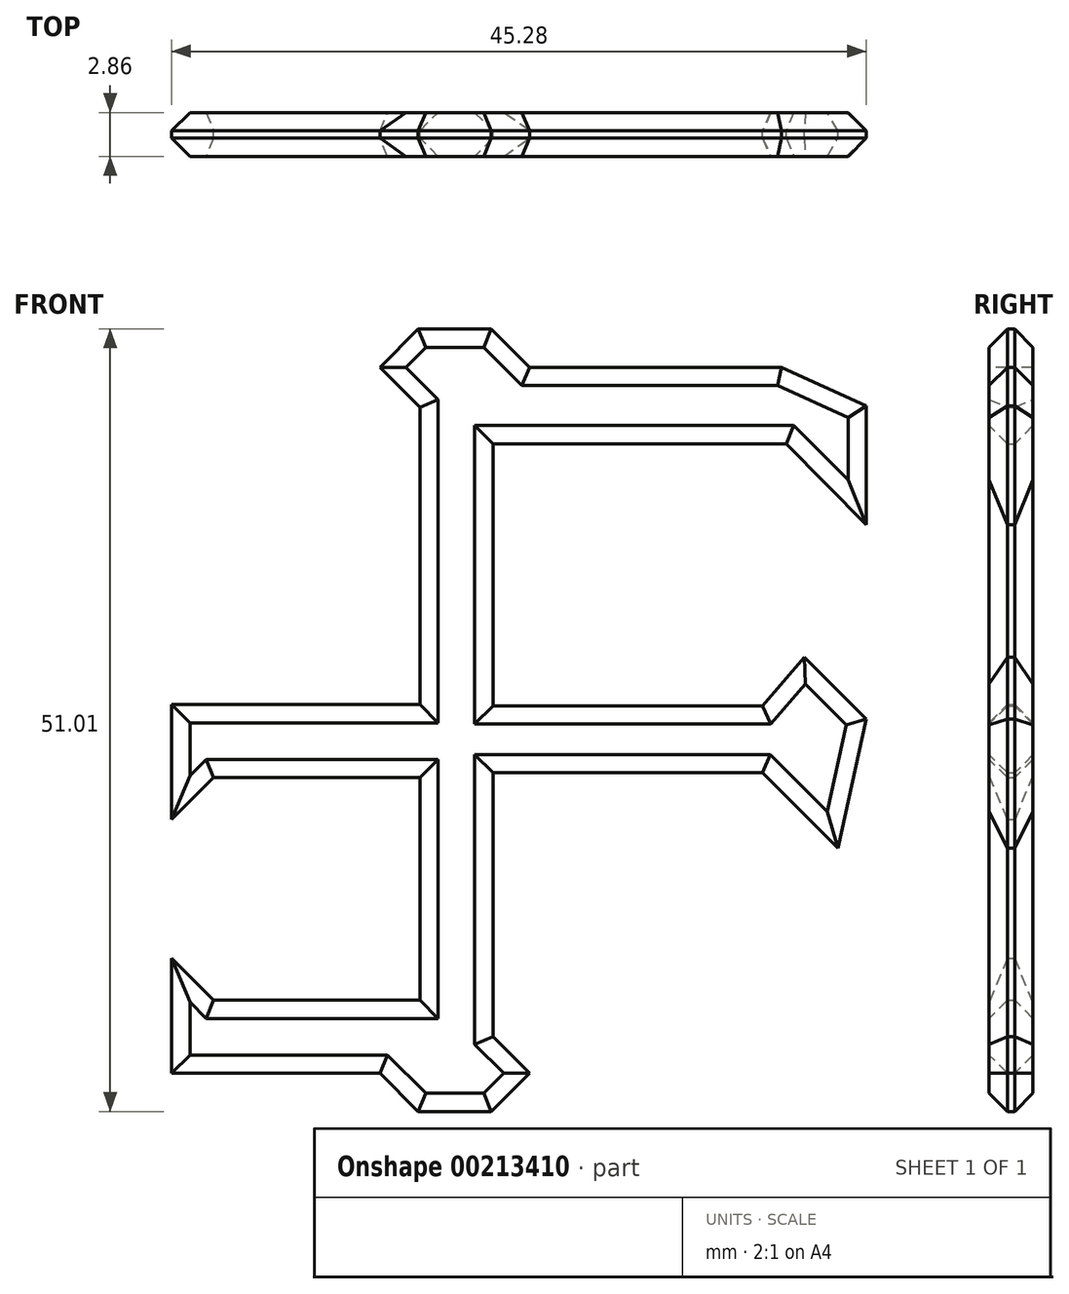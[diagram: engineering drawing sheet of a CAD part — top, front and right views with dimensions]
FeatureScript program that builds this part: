
annotation { "Feature Type Name" : "Feature", "Feature Type Description" : "" }
export const myFeature = defineFeature(function(context is Context, id is Id, definition is map)
    precondition{}
    {
        {
            var Q0;
            Q0=qCreatedBy(makeId("Front.planeOp"),FACE);
            var sketch = newSketch(context, id + "F0", { "sketchPlane" : qUnion([Q0])});
            skLineSegment(sketch, "E0", {"start": v(-3.18, 25.96) * mm, "end": v(-6.65, 29.43) * mm});
            skLineSegment(sketch, "E1", {"start": v(6.35, 29.43) * mm, "end": v(28.26, 29.43) * mm});
            skLineSegment(sketch, "E2", {"start": v(28.26, 29.43) * mm, "end": v(35.62, 26.07) * mm});
            skLineSegment(sketch, "E3", {"start": v(35.62, 15.75) * mm, "end": v(28.66, 22.79) * mm});
            skLineSegment(sketch, "E4", {"start": v(28.66, 22.79) * mm, "end": v(3.17, 22.79) * mm});
            skLineSegment(sketch, "E5", {"start": v(3.17, 22.79) * mm, "end": v(3.18, 0) * mm});
            skLineSegment(sketch, "E6", {"start": v(3.18, 0) * mm, "end": v(26.6, 0) * mm});
            skLineSegment(sketch, "E7", {"start": v(26.6, 0) * mm, "end": v(30.23, 4.24) * mm});
            skLineSegment(sketch, "E8", {"start": v(30.23, 4.24) * mm, "end": v(35.62, -1.15) * mm});
            skLineSegment(sketch, "E9", {"start": v(35.62, -1.15) * mm, "end": v(33.14, -12.36) * mm});
            skLineSegment(sketch, "E10", {"start": v(33.14, -12.36) * mm, "end": v(26.6, -5.82) * mm});
            skLineSegment(sketch, "E11", {"start": v(26.6, -5.82) * mm, "end": v(3.18, -5.82) * mm});
            skLineSegment(sketch, "E12", {"start": v(3.18, -5.82) * mm, "end": v(3.18, -28.75) * mm});
            skLineSegment(sketch, "E13", {"start": v(3.18, -28.75) * mm, "end": v(6.35, -31.93) * mm});
            skLineSegment(sketch, "E14", {"start": v(-6.65, 29.43) * mm, "end": v(-3.32, 32.76) * mm});
            skPoint(sketch, "E14.endSnap0", {"position": v(-3.32, 26.11) * mm});
            skLineSegment(sketch, "E15", {"start": v(-3.32, 32.76) * mm, "end": v(3.03, 32.76) * mm});
            skLineSegment(sketch, "E16", {"start": v(3.03, 32.76) * mm, "end": v(6.35, 29.43) * mm});
            skPoint(sketch, "E17.startSnap0", {"position": v(2.15, -36.37) * mm});
            skLineSegment(sketch, "E18", {"start": v(-6.65, -31.93) * mm, "end": v(-22.13, -31.93) * mm});
            skLineSegment(sketch, "E19", {"start": v(-22.13, -31.93) * mm, "end": v(-24.74, -31.93) * mm});
            skLineSegment(sketch, "E20", {"start": v(-24.74, -31.93) * mm, "end": v(-24.74, -21.93) * mm});
            skLineSegment(sketch, "E21", {"start": v(-24.74, -21.93) * mm, "end": v(-21.1, -25.58) * mm});
            skLineSegment(sketch, "E22", {"start": v(-21.1, -25.58) * mm, "end": v(-3.17, -25.58) * mm});
            skLineSegment(sketch, "E23", {"start": v(-3.17, -25.58) * mm, "end": v(-3.18, -6.24) * mm});
            skLineSegment(sketch, "E24", {"start": v(-3.18, -6.24) * mm, "end": v(-21.1, -6.24) * mm});
            skLineSegment(sketch, "E25", {"start": v(-21.1, -6.24) * mm, "end": v(-24.74, -9.88) * mm});
            skLineSegment(sketch, "E26", {"start": v(-24.74, -9.88) * mm, "end": v(-24.74, 0.11) * mm});
            skLineSegment(sketch, "E27", {"start": v(-24.74, 0.11) * mm, "end": v(-3.17, 0.11) * mm});
            skLineSegment(sketch, "E28", {"start": v(0, 22.79) * mm, "end": v(0, 0.11) * mm});
            skLineSegment(sketch, "E29", {"start": v(-3.18, 25.96) * mm, "end": v(-3.17, 0.11) * mm});
            skLineSegment(sketch, "E30", {"start": v(-6.65, -31.93) * mm, "end": v(-3.32, -35.25) * mm});
            skLineSegment(sketch, "E31", {"start": v(-3.32, -35.25) * mm, "end": v(3.03, -35.25) * mm});
            skLineSegment(sketch, "E32", {"start": v(3.03, -35.25) * mm, "end": v(6.35, -31.93) * mm});
            skPoint(sketch, "E33.orphan", {"position": v(-3.17, -31.93) * mm});
            skLineSegment(sketch, "E34", {"start": v(35.62, 26.07) * mm, "end": v(35.62, 15.75) * mm});
            skSolve(sketch);
        }
        {
            var Q0;
            Q0=makeQuery(id+"F0.imprint","IMPRINT",FACE,{"disambiguationData":[TD([[makeQuery(id+"F0.imprint","IMPRINT",EDGE,{"derivedFrom":sQuery(id+"F0.wireOp",EDGE,"E0")}),-1.0]])]});
            extrude(context, id + "F1", {"entities" : qUnion([Q0]), "depth" : 3.8 * mm});
        }
        {
            var Q0;
            Q0=makeQuery(id+"F1.opExtrude","CAP_FACE",FACE,{"disambiguationData":[OSD([sQuery(id+"F0.wireOp",EDGE,"E0"),sQuery(id+"F0.wireOp",EDGE,"E1"),sQuery(id+"F0.wireOp",EDGE,"E2"),sQuery(id+"F0.wireOp",EDGE,"E3"),sQuery(id+"F0.wireOp",EDGE,"E4"),sQuery(id+"F0.wireOp",EDGE,"E5"),sQuery(id+"F0.wireOp",EDGE,"E6"),sQuery(id+"F0.wireOp",EDGE,"E7"),sQuery(id+"F0.wireOp",EDGE,"E8"),sQuery(id+"F0.wireOp",EDGE,"E9"),sQuery(id+"F0.wireOp",EDGE,"E10"),sQuery(id+"F0.wireOp",EDGE,"E11"),sQuery(id+"F0.wireOp",EDGE,"E12"),sQuery(id+"F0.wireOp",EDGE,"E13"),sQuery(id+"F0.wireOp",EDGE,"E14"),sQuery(id+"F0.wireOp",EDGE,"E15"),sQuery(id+"F0.wireOp",EDGE,"E16"),sQuery(id+"F0.wireOp",EDGE,"E18"),sQuery(id+"F0.wireOp",EDGE,"E19"),sQuery(id+"F0.wireOp",EDGE,"E20"),sQuery(id+"F0.wireOp",EDGE,"E21"),sQuery(id+"F0.wireOp",EDGE,"E22"),sQuery(id+"F0.wireOp",EDGE,"E23"),sQuery(id+"F0.wireOp",EDGE,"E24"),sQuery(id+"F0.wireOp",EDGE,"E25"),sQuery(id+"F0.wireOp",EDGE,"E26"),sQuery(id+"F0.wireOp",EDGE,"E27"),sQuery(id+"F0.wireOp",EDGE,"E29"),sQuery(id+"F0.wireOp",EDGE,"E30"),sQuery(id+"F0.wireOp",EDGE,"E31"),sQuery(id+"F0.wireOp",EDGE,"E32"),sQuery(id+"F0.wireOp",EDGE,"E34")])],"isStart":false});
            var Q1;
            Q1=makeQuery(id+"F1.opExtrude","CAP_FACE",FACE,{"disambiguationData":[OSD([sQuery(id+"F0.wireOp",EDGE,"E0"),sQuery(id+"F0.wireOp",EDGE,"E1"),sQuery(id+"F0.wireOp",EDGE,"E2"),sQuery(id+"F0.wireOp",EDGE,"E3"),sQuery(id+"F0.wireOp",EDGE,"E4"),sQuery(id+"F0.wireOp",EDGE,"E5"),sQuery(id+"F0.wireOp",EDGE,"E6"),sQuery(id+"F0.wireOp",EDGE,"E7"),sQuery(id+"F0.wireOp",EDGE,"E8"),sQuery(id+"F0.wireOp",EDGE,"E9"),sQuery(id+"F0.wireOp",EDGE,"E10"),sQuery(id+"F0.wireOp",EDGE,"E11"),sQuery(id+"F0.wireOp",EDGE,"E12"),sQuery(id+"F0.wireOp",EDGE,"E13"),sQuery(id+"F0.wireOp",EDGE,"E14"),sQuery(id+"F0.wireOp",EDGE,"E15"),sQuery(id+"F0.wireOp",EDGE,"E16"),sQuery(id+"F0.wireOp",EDGE,"E18"),sQuery(id+"F0.wireOp",EDGE,"E19"),sQuery(id+"F0.wireOp",EDGE,"E20"),sQuery(id+"F0.wireOp",EDGE,"E21"),sQuery(id+"F0.wireOp",EDGE,"E22"),sQuery(id+"F0.wireOp",EDGE,"E23"),sQuery(id+"F0.wireOp",EDGE,"E24"),sQuery(id+"F0.wireOp",EDGE,"E25"),sQuery(id+"F0.wireOp",EDGE,"E26"),sQuery(id+"F0.wireOp",EDGE,"E27"),sQuery(id+"F0.wireOp",EDGE,"E29"),sQuery(id+"F0.wireOp",EDGE,"E30"),sQuery(id+"F0.wireOp",EDGE,"E31"),sQuery(id+"F0.wireOp",EDGE,"E32"),sQuery(id+"F0.wireOp",EDGE,"E34")])],"isStart":true});
            chamfer(context, id + "F2", {"entities" : qUnion([Q0, Q1]), "width" : 1.59 * mm, "tangentPropagation" : true});
        }
        {
            var Q0;
            Q0=makeQuery(id+"F1.opExtrude","SWEPT_BODY",BODY,{"disambiguationData":[OSD([sQuery(id+"F0.wireOp",EDGE,"E0"),sQuery(id+"F0.wireOp",EDGE,"E1"),sQuery(id+"F0.wireOp",EDGE,"E2"),sQuery(id+"F0.wireOp",EDGE,"E3"),sQuery(id+"F0.wireOp",EDGE,"E4"),sQuery(id+"F0.wireOp",EDGE,"E5"),sQuery(id+"F0.wireOp",EDGE,"E6"),sQuery(id+"F0.wireOp",EDGE,"E7"),sQuery(id+"F0.wireOp",EDGE,"E8"),sQuery(id+"F0.wireOp",EDGE,"E9"),sQuery(id+"F0.wireOp",EDGE,"E10"),sQuery(id+"F0.wireOp",EDGE,"E11"),sQuery(id+"F0.wireOp",EDGE,"E12"),sQuery(id+"F0.wireOp",EDGE,"E13"),sQuery(id+"F0.wireOp",EDGE,"E14"),sQuery(id+"F0.wireOp",EDGE,"E15"),sQuery(id+"F0.wireOp",EDGE,"E16"),sQuery(id+"F0.wireOp",EDGE,"E18"),sQuery(id+"F0.wireOp",EDGE,"E19"),sQuery(id+"F0.wireOp",EDGE,"E20"),sQuery(id+"F0.wireOp",EDGE,"E21"),sQuery(id+"F0.wireOp",EDGE,"E22"),sQuery(id+"F0.wireOp",EDGE,"E23"),sQuery(id+"F0.wireOp",EDGE,"E24"),sQuery(id+"F0.wireOp",EDGE,"E25"),sQuery(id+"F0.wireOp",EDGE,"E26"),sQuery(id+"F0.wireOp",EDGE,"E27"),sQuery(id+"F0.wireOp",EDGE,"E29"),sQuery(id+"F0.wireOp",EDGE,"E30"),sQuery(id+"F0.wireOp",EDGE,"E31"),sQuery(id+"F0.wireOp",EDGE,"E32"),sQuery(id+"F0.wireOp",EDGE,"E34")])]});
            var Q1;
            Q1=qCreatedBy(makeId("Origin.pointOp"),VERTEX);
            transform(context, id + "F3", {"entities" : qUnion([Q0]), "transformType" : TransformType.SCALE_UNIFORMLY, "scale" : .75, "scalePoint" : qUnion([Q1]), "makeCopy" : false});
        }
    });
